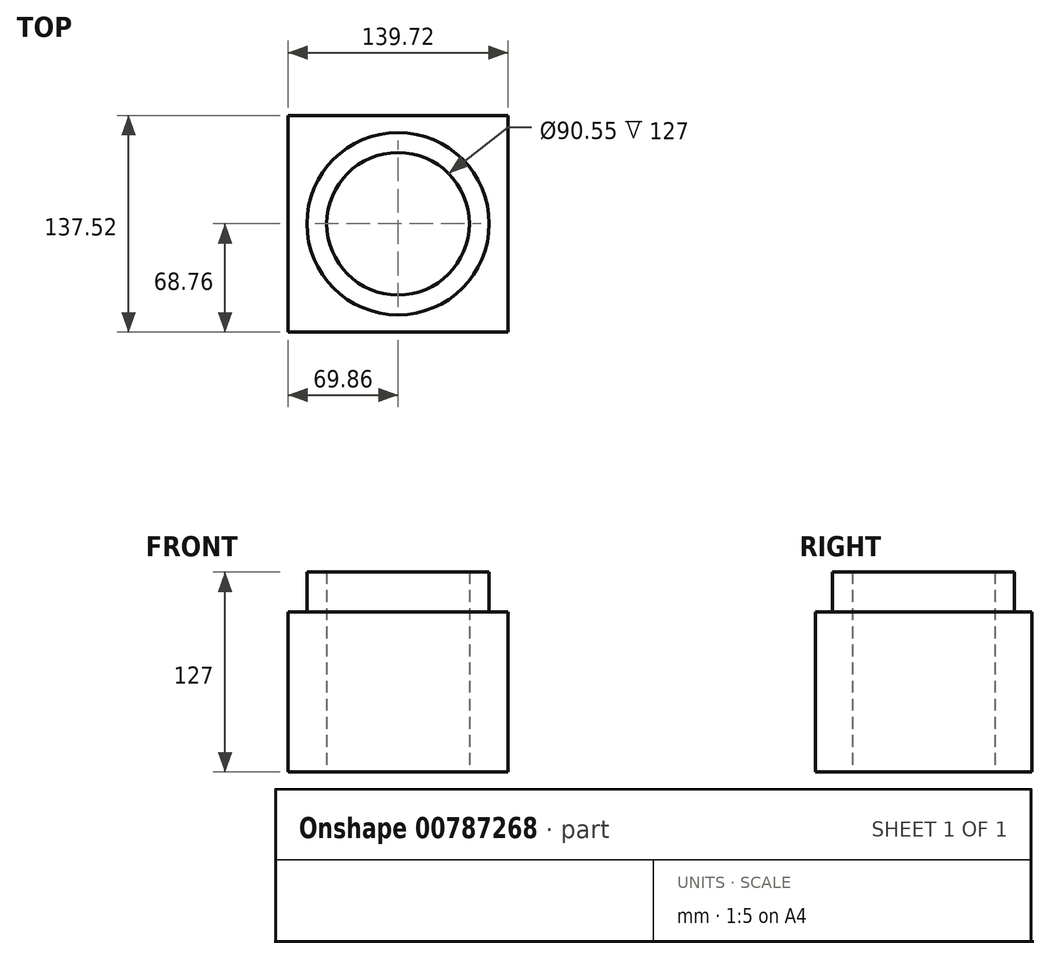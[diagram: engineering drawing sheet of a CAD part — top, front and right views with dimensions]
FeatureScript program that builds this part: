
annotation { "Feature Type Name" : "Feature", "Feature Type Description" : "" }
export const myFeature = defineFeature(function(context is Context, id is Id, definition is map)
    precondition{}
    {
        {
            var Q0;
            Q0=qCreatedBy(makeId("Top.planeOp"),FACE);
            var sketch = newSketch(context, id + "F0", { "sketchPlane" : qUnion([Q0])});
            skLineSegment(sketch, "E0.bottom", {"start": v(69.86, -68.76) * mm, "end": v(-69.86, -68.76) * mm});
            skLineSegment(sketch, "E0.top", {"start": v(69.86, 68.76) * mm, "end": v(-69.86, 68.76) * mm});
            skLineSegment(sketch, "E0.left", {"start": v(69.86, -68.76) * mm, "end": v(69.86, 68.76) * mm});
            skLineSegment(sketch, "E0.right", {"start": v(-69.86, -68.76) * mm, "end": v(-69.86, 68.76) * mm});
            skPoint(sketch, "E0.middle", {"position": v(0, 0) * mm});
            skCircle(sketch, "E1", {"center": v(0, 0) * mm, "radius": 45.27 * mm});
            skCircle(sketch, "E2", {"center": v(0, 0) * mm, "radius": 57.88 * mm});
            skPoint(sketch, "E3.orphan", {"position": v(0, -68.76) * mm});
            skPoint(sketch, "E4.start.orphan", {"position": v(0, 68.76) * mm});
            skSolve(sketch);
        }
        {
            var Q0;
            Q0=makeQuery(id+"F0.imprint","IMPRINT",FACE,{"disambiguationData":[TD([[makeQuery(id+"F0.imprint","IMPRINT",EDGE,{"derivedFrom":sQuery(id+"F0.wireOp",EDGE,"E0.bottom")}),-1.0]])]});
            extrude(context, id + "F1", {"entities" : qUnion([Q0]), "depth" : 101.6 * mm, "offsetDistance" : 25.4 * mm});
        }
        {
            var Q0;
            Q0=makeQuery(id+"F0.imprint","IMPRINT",FACE,{"disambiguationData":[TD([[makeQuery(id+"F0.imprint","IMPRINT",EDGE,{"derivedFrom":sQuery(id+"F0.wireOp",EDGE,"E1")}),-1.0]])]});
            extrude(context, id + "F2", {"entities" : qUnion([Q0]), "operationType" : NewBodyOperationType.ADD, "depth" : 127 * mm, "offsetDistance" : 25.4 * mm});
        }
    });
